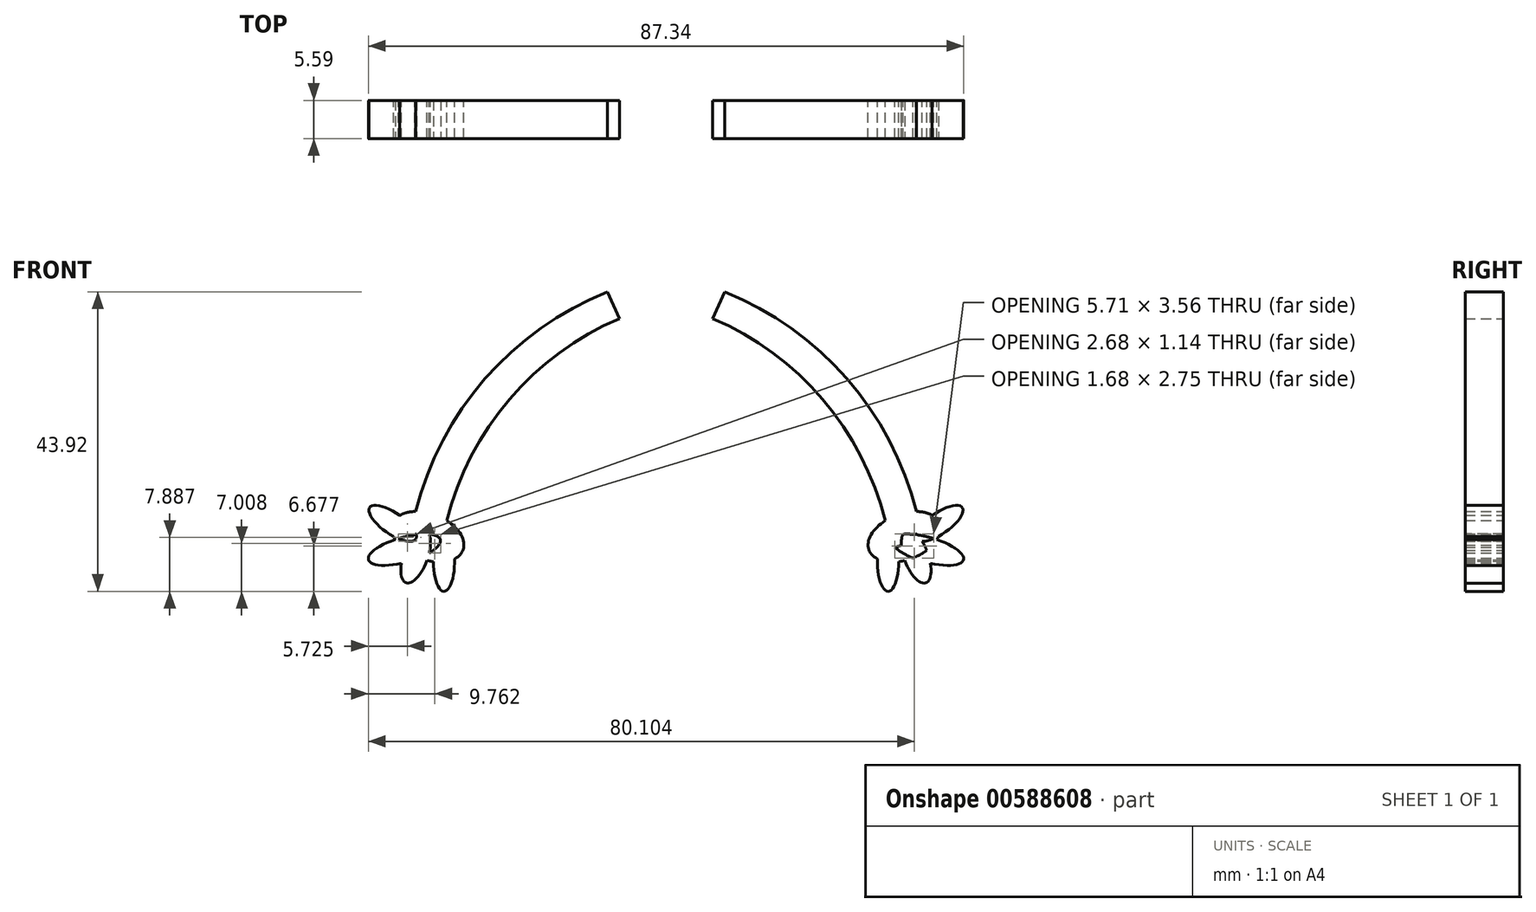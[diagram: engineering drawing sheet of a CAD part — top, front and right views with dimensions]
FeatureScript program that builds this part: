
annotation { "Feature Type Name" : "Feature", "Feature Type Description" : "" }
export const myFeature = defineFeature(function(context is Context, id is Id, definition is map)
    precondition{}
    {
        {
            var Q0;
            Q0=qCreatedBy(makeId("Front.planeOp"),FACE);
            var sketch = newSketch(context, id + "F0", { "sketchPlane" : qUnion([Q0])});
            skArc(sketch, "E0", {"start": v(36.9, 12.9) * mm, "mid": v(26.77, 32.78) * mm, "end": v(8.62, 45.78) * mm});
            skArc(sketch, "E1", {"start": v(32.27, 11.82) * mm, "mid": v(23.11, 29.85) * mm, "end": v(6.85, 41.87) * mm});
            skLineSegment(sketch, "E2", {"start": v(8.62, 45.78) * mm, "end": v(6.85, 41.87) * mm});
            skLineSegment(sketch, "E3", {"start": v(36.9, 12.9) * mm, "end": v(32.27, 11.82) * mm});
            skEllipse(sketch, "E4", {"center": v(34.94, 9.87) * mm, "majorRadius": 5.51 * mm, "minorRadius": 3.37 * mm, "majorAxis": v(-0.93, -0.35)});
            skEllipse(sketch, "E5", {"center": v(40.1, 11.82) * mm, "majorRadius": 4.1 * mm, "minorRadius": 1.56 * mm, "majorAxis": v(0.83, 0.56)});
            skEllipticalArc(sketch, "E6", {});
            skPoint(sketch, "E6.centerSnap0", {"position": v(36.72, 9.51) * mm});
            skEllipticalArc(sketch, "E7", {});
            skEllipticalArc(sketch, "E8", {});
            skPoint(sketch, "E8.centerSnap0", {"position": v(38.37, 7.57) * mm});
            skArc(sketch, "E9", {"start": v(33.58, 8.33) * mm, "mid": v(34.07, 8.47) * mm, "end": v(34.55, 8.62) * mm});
            skPoint(sketch, "E9.startSnap0", {"position": v(29.78, 7.91) * mm});
            skArc(sketch, "E10.trimOffspring", {"start": v(36.72, 9.51) * mm, "mid": v(37.18, 9.76) * mm, "end": v(37.64, 10.02) * mm});
            skLineSegment(sketch, "E11", {"start": v(37.64, 10.02) * mm, "end": v(37.39, 9.19) * mm});
            skEllipticalArc(sketch, "E12.trimOffspring", {});
            skArc(sketch, "E13.MirrorCS", {"start": v(-36.9, 12.9) * mm, "mid": v(-36.81, 13.23) * mm, "end": v(-36.73, 13.58) * mm});
            skArc(sketch, "E14.MirrorCS", {"start": v(-32.27, 11.82) * mm, "mid": v(-32.22, 12.03) * mm, "end": v(-32.17, 12.24) * mm});
            skPoint(sketch, "E15.MirrorP", {"position": v(-36.72, 9.51) * mm});
            skEllipticalArc(sketch, "E16.MirrorCS", {});
            skEllipticalArc(sketch, "E17.MirrorCS", {});
            skEllipticalArc(sketch, "E18.MirrorCS", {});
            skEllipticalArc(sketch, "E19.MirrorCS", {});
            skEllipticalArc(sketch, "E20.MirrorCS", {});
            skEllipticalArc(sketch, "E21.MirrorCS", {});
            skEllipticalArc(sketch, "E22.MirrorC", {});
            skPoint(sketch, "E23.MirrorP", {"position": v(-29.78, 7.91) * mm});
            skPoint(sketch, "E24.MirrorP", {"position": v(-38.37, 7.57) * mm});
            skEllipticalArc(sketch, "E25.MirrorC", {});
            skPoint(sketch, "E26.orphan", {"position": v(-8.62, 45.78) * mm});
            skPoint(sketch, "E27.orphan", {"position": v(-6.85, 41.87) * mm});
            skPoint(sketch, "E28.orphan", {"position": v(-31.14, 7.91) * mm});
            skEllipticalArc(sketch, "E29.trimOffspring", {});
            skPoint(sketch, "E30.MirrorCS.end.orphan", {"position": v(-32.27, 11.82) * mm});
            skPoint(sketch, "E30.MirrorCS.start.orphan", {"position": v(-36.9, 12.9) * mm});
            skPoint(sketch, "E31.MirrorCS.start.orphan", {"position": v(-33.9, 8.42) * mm});
            skPoint(sketch, "E32.trimOffspring.end.orphan", {"position": v(-34.75, 10.24) * mm});
            skPoint(sketch, "E33.trimOffspring.end.orphan", {"position": v(-36.24, 6.76) * mm});
            skEllipticalArc(sketch, "E34.trimOffspring", {});
            skEllipticalArc(sketch, "E35.trimOffspring", {});
            skEllipticalArc(sketch, "E36.trimOffspring", {});
            skEllipticalArc(sketch, "E37.trimOffspring", {});
            skEllipticalArc(sketch, "E38.trimOffspring", {});
            skArc(sketch, "E39.MirrorCS", {"start": v(-32.27, 11.82) * mm, "mid": v(-23.11, 29.85) * mm, "end": v(-6.85, 41.87) * mm});
            skArc(sketch, "E40.MirrorCS", {"start": v(-36.9, 12.9) * mm, "mid": v(-26.77, 32.78) * mm, "end": v(-8.62, 45.78) * mm});
            skEllipse(sketch, "E41.MirrorC", {"center": v(-34.94, 9.87) * mm, "majorRadius": 5.51 * mm, "minorRadius": 3.37 * mm, "majorAxis": v(0.93, -0.35)});
            skEllipse(sketch, "E42.MirrorC", {"center": v(-40.1, 11.82) * mm, "majorRadius": 4.1 * mm, "minorRadius": 1.56 * mm, "majorAxis": v(-0.83, 0.56)});
            skEllipticalArc(sketch, "E43.MirrorCS", {});
            skEllipticalArc(sketch, "E44.MirrorCS", {});
            skLineSegment(sketch, "E45.MirrorCS", {"start": v(-36.9, 12.9) * mm, "end": v(-32.27, 11.82) * mm});
            skLineSegment(sketch, "E46.MirrorCS", {"start": v(-8.62, 45.78) * mm, "end": v(-6.85, 41.87) * mm});
            const initialGuessF0  = {"E6": [0.036715712398290634, 0.0069598389324304, 0.34668754552043457, -0.9379806745242766, 0.004102791216030547, 0.0017634419487027235, 3.5532795904212215, 2.45066338610622], "E7": [0.032570763180655334, 0.006192290333767151, 0, -1, 0.004330476796155338, 0.0015552194414240985, 4.303989425013528, 2.1113762744301265], "E8": [0.03836978686681922, 0.007967100968243832, 0.9630128307678893, -0.26945553951703516, 0.0054829112023282, 0.0018298658840317972, 3.678942336274236, 2.4151242253403047], "E12.trimOffspring": [0.03836978686681922, 0.007967100968243832, 0.9630128307678893, -0.26945553951703516, 0.0054829112023282, 0.0018298658840317972, 4.3929880742481355, 1.9968428936497447], "E16.MirrorCS": [-0.03836978686681922, 0.007967100968243832, -0.9630128307678893, -0.26945553951703516, 0.0054829112023282, 0.0018298658840317972, 4.286342413529842, 4.879054719507128], "E16.MirrorCS": [-0.03836978686681922, 0.007967100968243832, -0.9630128307678893, -0.26945553951703516, 0.0054829112023282, 0.0018298658840317972, 4.286342413529842, 4.879054719507128], "E17.MirrorCS": [-0.032570763180655334, 0.006192290333767151, 0, -1, 0.004330476796155338, 0.0015552194414240985, 4.17180903274946, 4.707476292847949], "E17.MirrorCS": [-0.032570763180655334, 0.006192290333767151, 0, -1, 0.004330476796155338, 0.0015552194414240985, 4.17180903274946, 4.707476292847949], "E18.MirrorCS": [-0.032570763180655334, 0.006192290333767151, 0, -1, 0.004330476796155338, 0.0015552194414240985, 4.17180903274946, 1.9791958821660582], "E19.MirrorCS": [-0.036715712398290634, 0.0069598389324304, -0.34668754552043457, -0.9379806745242766, 0.004102791216030547, 0.0017634419487027235, 3.8325219210733663, 5.12544536800662], "E19.MirrorCS": [-0.036715712398290634, 0.0069598389324304, -0.34668754552043457, -0.9379806745242766, 0.004102791216030547, 0.0017634419487027235, 3.8325219210733663, 5.12544536800662], "E20.MirrorCS": [-0.03836978686681922, 0.007967100968243832, -0.9630128307678893, -0.26945553951703516, 0.0054829112023282, 0.0018298658840317972, 4.286342413529842, 3.8680610818392815], "E21.MirrorCS": [-0.03836978686681922, 0.007967100968243832, -0.9630128307678893, -0.26945553951703516, 0.0054829112023282, 0.0018298658840317972, 4.286342413529842, 4.793175879320614], "E22.MirrorC": [-0.040093906223773956, 0.011823699809610844, -0.8253067645560311, 0.5646846415283985, 0.004093258374418634, 0.0015580378191070627, 2.058726233668546, 3.597801392940515], "E25.MirrorC": [-0.03493770211935043, 0.009867900051176548, 0.9349976344576945, -0.3546539490242787, 0.005514670748246502, 0.0033717592167461217, 3.141592653589793, 0], "E29.trimOffspring": [-0.03836978686681922, 0.007967100968243832, -0.9630128307678893, -0.26945553951703516, 0.0054829112023282, 0.0018298658840317972, 1.3961602990695703, 1.890197232931451], "E29.trimOffspring": [-0.03836978686681922, 0.007967100968243832, -0.9630128307678893, -0.26945553951703516, 0.0054829112023282, 0.0018298658840317972, 1.3961602990695703, 1.890197232931451], "E29.trimOffspring": [-0.03836978686681922, 0.007967100968243832, -0.9630128307678893, -0.26945553951703516, 0.0054829112023282, 0.0018298658840317972, 1.3961602990695703, 1.890197232931451], "E34.trimOffspring": [-0.03836978686681922, 0.007967100968243832, -0.9630128307678893, -0.26945553951703516, 0.0054829112023282, 0.0018298658840317972, 4.793175879320614, 4.879054719507128], "E35.trimOffspring": [-0.03836978686681922, 0.007967100968243832, -0.9630128307678893, -0.26945553951703516, 0.0054829112023282, 0.0018298658840317972, 4.793175879320614, 3.8680610818392815], "E36.trimOffspring": [-0.03493770211935043, 0.009867900051176548, 0.9349976344576945, -0.3546539490242787, 0.005514670748246502, 0.0033717592167461217, 3.8070931244459203, 4.690961245364948], "E37.trimOffspring": [-0.03493770211935043, 0.009867900051176548, 0.9349976344576945, -0.3546539490242787, 0.005514670748246502, 0.0033717592167461217, 5.094243427355889, 0], "E38.trimOffspring": [-0.032570763180655334, 0.006192290333767151, 0, -1, 0.004330476796155338, 0.0015552194414240985, 1.669974309147972, 1.9791958821660582], "E38.trimOffspring": [-0.032570763180655334, 0.006192290333767151, 0, -1, 0.004330476796155338, 0.0015552194414240985, 1.669974309147972, 1.9791958821660582], "E43.MirrorCS": [-0.03836978686681922, 0.007967100968243832, -0.9630128307678893, -0.26945553951703516, 0.0054829112023282, 0.0018298658840317972, 4.286342413529842, 1.8901972329314507], "E44.MirrorCS": [-0.036715712398290634, 0.0069598389324304, -0.34668754552043457, -0.9379806745242766, 0.004102791216030547, 0.0017634419487027235, 3.8325219210733663, 2.7299057167583656], "E18.MirrorCS": [-0.032570763180655334, 0.006192290333767151, 0, -1, 0.004330476796155338, 0.0015552194414240985, 4.17180903274946, 1.9791958821660582]};
            skSetInitialGuess(sketch, initialGuessF0);
            skSolve(sketch);
        }
        {
            var Q0;
            Q0 = qSketchRegion(id + "F0", true);
            extrude(context, id + "F1", {"entities" : qUnion([Q0]), "depth" : 5.6 * mm, "offsetDistance" : 25.4 * mm});
        }
    });
